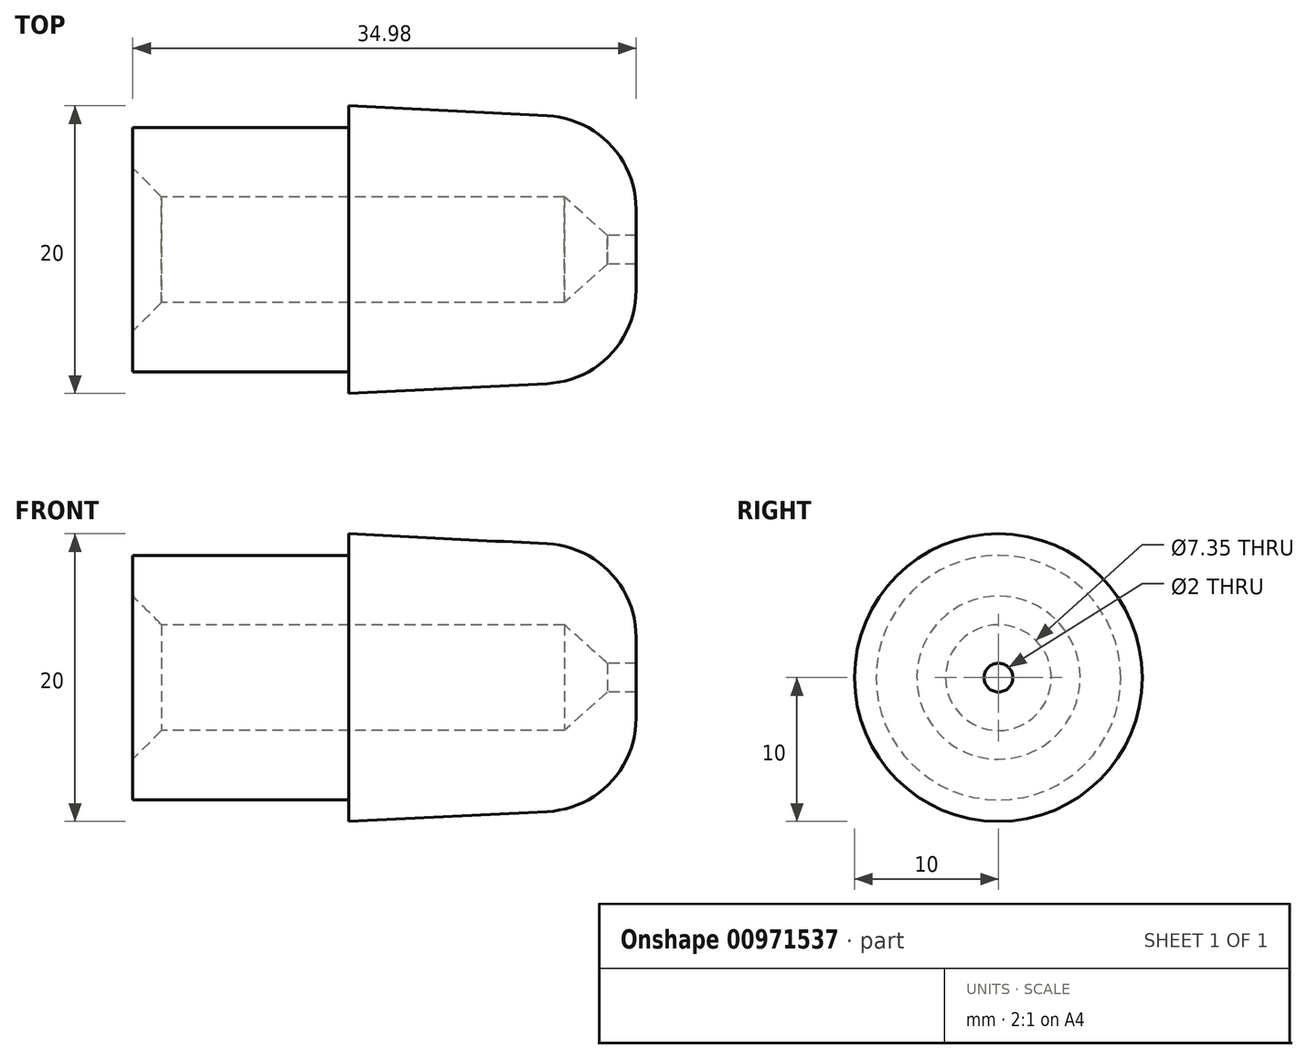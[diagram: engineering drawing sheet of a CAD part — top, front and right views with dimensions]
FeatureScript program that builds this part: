
annotation { "Feature Type Name" : "Feature", "Feature Type Description" : "" }
export const myFeature = defineFeature(function(context is Context, id is Id, definition is map)
    precondition{}
    {
        {
            var Q0;
            Q0=qCreatedBy(makeId("Top.planeOp"),FACE);
            var sketch = newSketch(context, id + "F0", { "sketchPlane" : qUnion([Q0])});
            skLineSegment(sketch, "E0", {"start": v(-130.87, 0) * mm, "end": v(141.93, 0) * mm, "construction": true});
            skLineSegment(sketch, "E1", {"start": v(-74.08, 3.67) * mm, "end": v(-44.08, 3.67) * mm});
            skLineSegment(sketch, "E2", {"start": v(-44.08, 3.67) * mm, "end": v(-41.1, 1) * mm});
            skLineSegment(sketch, "E3", {"start": v(-41.1, 1) * mm, "end": v(-39.1, 1) * mm});
            skLineSegment(sketch, "E4", {"start": v(-39.1, 1) * mm, "end": v(-39.1, 9) * mm});
            skLineSegment(sketch, "E5", {"start": v(-39.1, 9) * mm, "end": v(-59.08, 10) * mm});
            skLineSegment(sketch, "E6", {"start": v(-74.08, 3.67) * mm, "end": v(-74.08, 8.5) * mm});
            skLineSegment(sketch, "E7", {"start": v(-74.08, 8.5) * mm, "end": v(-59.08, 8.5) * mm});
            skLineSegment(sketch, "E8", {"start": v(-59.08, 10) * mm, "end": v(-59.08, 8.5) * mm});
            skSolve(sketch);
        }
        {
            var Q0;
            Q0=makeQuery(id+"F0.imprint","IMPRINT",FACE,{"disambiguationData":[TD([[makeQuery(id+"F0.imprint","IMPRINT",EDGE,{"derivedFrom":sQuery(id+"F0.wireOp",EDGE,"E1")}),1.0]])]});
            var Q1;
            Q1=sQuery(id+"F0.wireOp",EDGE,"E0");
            revolve(context, id + "F1", {"entities" : qUnion([Q0]), "axis" : qUnion([Q1]), "revolveType" : RevolveType.FULL, "surfaceOperationType" : NewSurfaceOperationType.NEW});
        }
        {
            var Q0;
            Q0=makeQuery(id+"F1.opRevolve","SWEPT_EDGE",EDGE,{"disambiguationData":[OSD([sQuery(id+"F0.wireOp",EDGE,"E4"),sQuery(id+"F0.wireOp",EDGE,"E5")])]});
            fillet(context, id + "F2", {"entities" : qUnion([Q0]), "radius" : 6.5 * mm, "tangentPropagation" : true, "allowEdgeOverflow" : false});
        }
        {
            var Q0;
            Q0=makeQuery(id+"F1.opRevolve","SWEPT_EDGE",EDGE,{"disambiguationData":[OSD([sQuery(id+"F0.wireOp",EDGE,"E1"),sQuery(id+"F0.wireOp",EDGE,"E6")])]});
            chamfer(context, id + "F3", {"entities" : qUnion([Q0]), "width" : 2 * mm, "tangentPropagation" : true});
        }
    });
